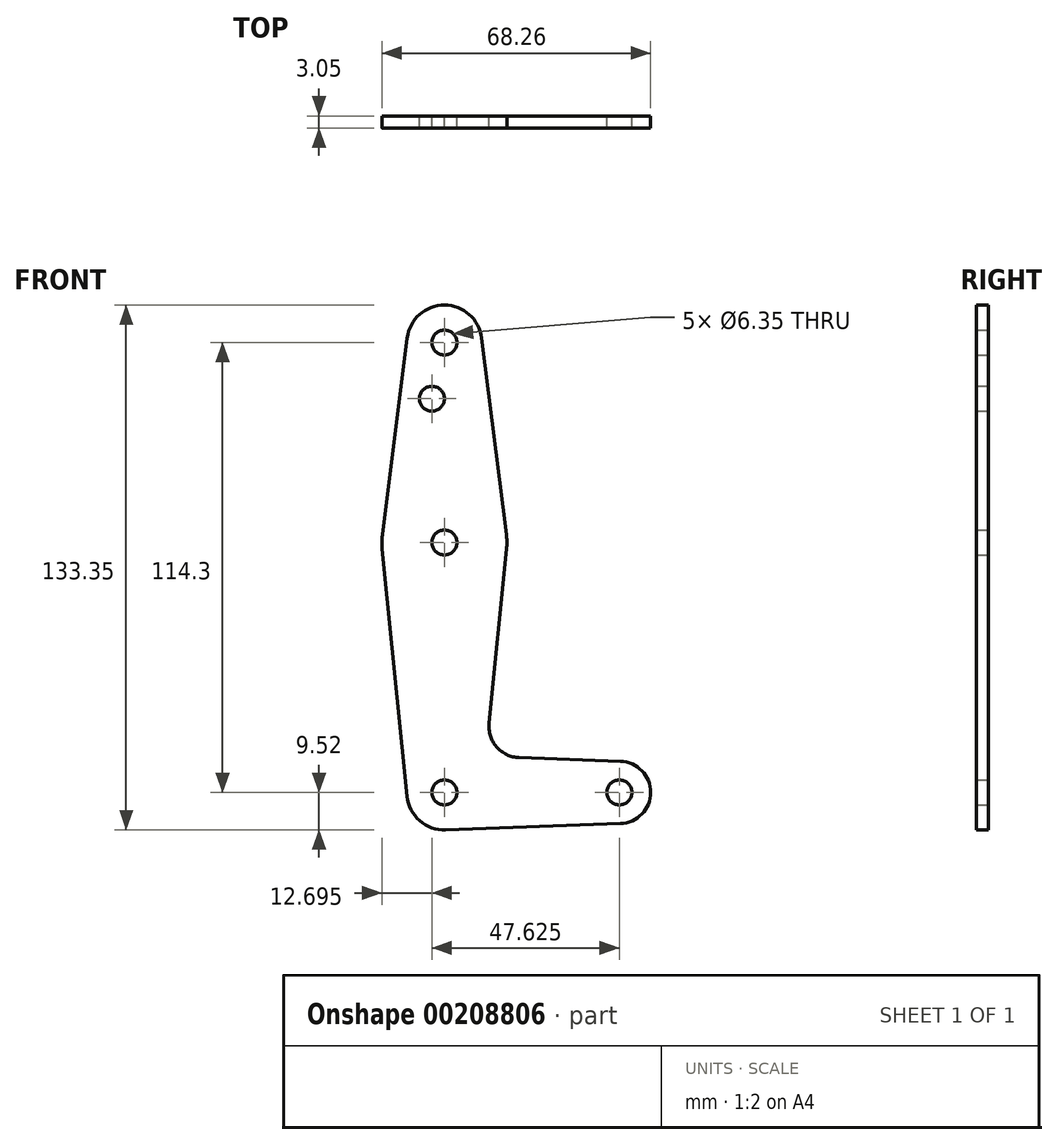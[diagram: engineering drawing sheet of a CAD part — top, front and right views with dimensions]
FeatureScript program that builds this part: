
annotation { "Feature Type Name" : "Feature", "Feature Type Description" : "" }
export const myFeature = defineFeature(function(context is Context, id is Id, definition is map)
    precondition{}
    {
        {
            var Q0;
            Q0=qCreatedBy(makeId("Front.planeOp"),FACE);
            var sketch = newSketch(context, id + "F0", { "sketchPlane" : qUnion([Q0])});
            skCircle(sketch, "E0", {"center": v(0, 0) * mm, "radius": 9.53 * mm});
            skLineSegment(sketch, "E1", {"start": v(0, 0) * mm, "end": v(0, 114.3) * mm, "construction": true});
            skLineSegment(sketch, "E2", {"start": v(0, 0) * mm, "end": v(44.45, 0) * mm, "construction": true});
            skCircle(sketch, "E3", {"center": v(0, 114.3) * mm, "radius": 9.53 * mm});
            skCircle(sketch, "E4", {"center": v(0, 63.5) * mm, "radius": 15.88 * mm});
            skCircle(sketch, "E5", {"center": v(44.45, 0) * mm, "radius": 7.94 * mm});
            skLineSegment(sketch, "E6", {"start": v(-9.45, 115.5) * mm, "end": v(-15.75, 65.48) * mm});
            skLineSegment(sketch, "E7", {"start": v(9.45, 115.5) * mm, "end": v(15.75, 65.48) * mm});
            skLineSegment(sketch, "E8", {"start": v(-15.8, 61.91) * mm, "end": v(-9.48, -0.95) * mm});
            skPoint(sketch, "E9.startSnap0", {"position": v(0, 57.15) * mm});
            skLineSegment(sketch, "E10", {"start": v(18.97, 8.85) * mm, "end": v(44.73, 7.93) * mm});
            skLineSegment(sketch, "E11", {"start": v(0.34, -9.52) * mm, "end": v(44.73, -7.93) * mm});
            skLineSegment(sketch, "E12", {"start": v(11.34, 17.6) * mm, "end": v(15.8, 61.91) * mm});
            skArc(sketch, "E13.filletArc", {"start": v(11.34, 17.6) * mm, "mid": v(13.26, 11.57) * mm, "end": v(18.97, 8.85) * mm});
            skCircle(sketch, "E14", {"center": v(0, 114.3) * mm, "radius": 3.18 * mm});
            skCircle(sketch, "E15", {"center": v(0, 63.5) * mm, "radius": 3.18 * mm});
            skCircle(sketch, "E16", {"center": v(0, 0) * mm, "radius": 3.18 * mm});
            skCircle(sketch, "E17", {"center": v(44.45, 0) * mm, "radius": 3.18 * mm});
            skCircle(sketch, "E18", {"center": v(-3.18, 100.03) * mm, "radius": 3.18 * mm});
            skSolve(sketch);
        }
        {
            var Q0;
            Q0 = qSketchRegion(id + "F0", true);
            extrude(context, id + "F1", {"entities" : qUnion([Q0]), "depth" : 3.05 * mm});
        }
    });
